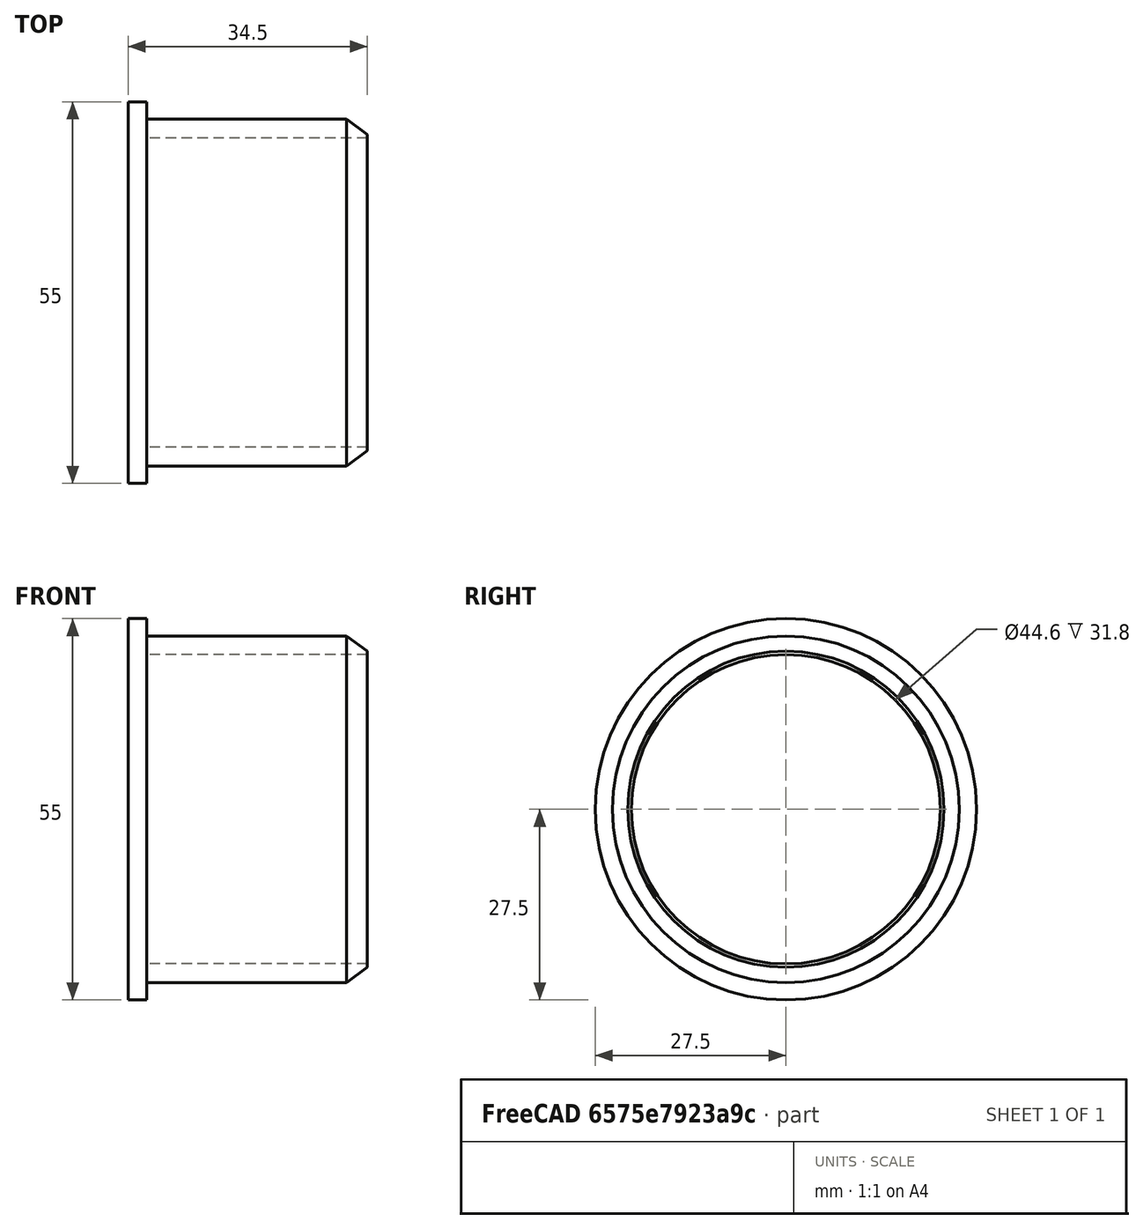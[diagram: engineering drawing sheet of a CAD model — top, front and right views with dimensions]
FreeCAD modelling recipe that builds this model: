
FCSTD DOCUMENT  (FreeCAD 0.22R38385 (Git))
Label: HtMuffenstopfenDn50
License: All rights reserved
objects: Sketcher::SketchObject×1, PartDesign::Revolution×1, PartDesign::Body×1
note: 6 computed .brp shape members not serialized (recipe doc carries the construction recipe); baked Part::Feature solids carry a one-line shape summary decoded from their .brp

FEATURE [Sketcher::SketchObject] Sketch
  ArcFitTolerance = 1e-06
  AttachmentSupport = -> [XZ_Plane]
  FullyConstrained = false
  MakeInternals = false
  MapMode = 5
  Placement = pos=(0,0,0) rot=(1,0,0;1.5708rad)
  sketch-geometry (9):
    g0: LineSegment StartX=0.0406645 StartY=0 StartZ=0 EndX=0.0406645 EndY=27.5 EndZ=0
    g1: LineSegment StartX=0.0406645 StartY=27.5 StartZ=0 EndX=2.74066 EndY=27.5 EndZ=0
    g2: LineSegment StartX=2.74066 StartY=27.5 StartZ=0 EndX=2.74066 EndY=25 EndZ=0
    g3: LineSegment StartX=2.74066 StartY=25 StartZ=0 EndX=31.5407 EndY=25 EndZ=0
    g4: LineSegment StartX=31.5407 StartY=25 StartZ=0 EndX=34.5407 EndY=22.8 EndZ=0
    g5: LineSegment StartX=34.5407 StartY=22.8 StartZ=0 EndX=34.5407 EndY=22.3 EndZ=0
    g6: LineSegment StartX=34.5407 StartY=22.3 StartZ=0 EndX=2.74066 EndY=22.3 EndZ=0
    g7: LineSegment StartX=2.74066 StartY=22.3 StartZ=0 EndX=2.74066 EndY=0 EndZ=0
    g8: LineSegment StartX=2.74066 StartY=0 StartZ=0 EndX=0.0406645 EndY=0 EndZ=0
  constraints (26):
    c: PointOnObject(g0,g-1)
    c: Vertical(g0)
    c: Coincident(g0,g1)
    c: Horizontal(g1)
    c: Coincident(g1,g2)
    c: Vertical(g2)
    c: Coincident(g2,g3)
    c: Horizontal(g3)
    c: Coincident(g3,g4)
    c: Coincident(g4,g5)
    c: Coincident(g5,g6)
    c: Horizontal(g6)
    c: Coincident(g6,g7)
    c: Vertical(g7)
    c: Coincident(g7,g8)
    c: Coincident(g8,g0)
    c: DistanceY(g0,g0) = 27.5
    c: Horizontal(g8)
    c: DistanceX(g8,g8) = 2.7
    c: Vertical(g7,g1)
    c: DistanceY(g6,g2) = 2.7
    c: DistanceY(g7,g2) = 25
    c: DistanceX(g0,g5) = 34.5
    c: Vertical(g5)
    c: Distance(g5,g5) = 0.5
    c: DistanceX(g3,g5) = 3
FEATURE [PartDesign::Revolution] Revolution
  Angle = 360
  Angle2 = 60
  Axis = (1,0,0)
  Base = (0,0,0)
  Placement = pos=(0,0,0) rot=(1,0,0;1.5708rad)
  Profile = -> Sketch
  ReferenceAxis = -> X_Axis
  Suppressed = false
  Type = 0
FEATURE [PartDesign::Body] Body
  AllowCompound = false
  Group = -> [Sketch,Revolution]
  Origin = -> Origin
  Tip = -> Revolution
